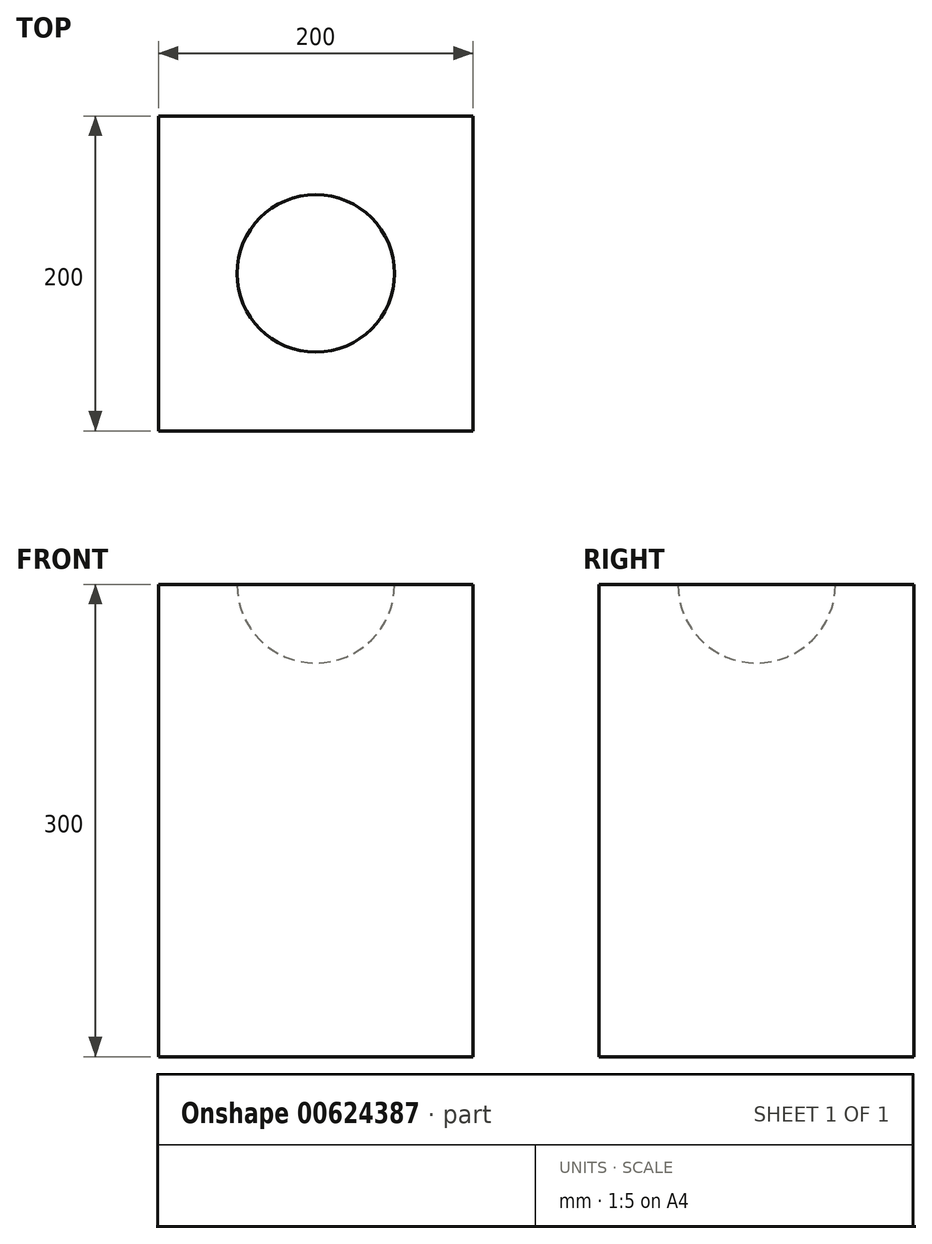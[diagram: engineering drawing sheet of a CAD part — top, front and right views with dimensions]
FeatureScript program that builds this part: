
annotation { "Feature Type Name" : "Feature", "Feature Type Description" : "" }
export const myFeature = defineFeature(function(context is Context, id is Id, definition is map)
    precondition{}
    {
        {
            var Q0;
            Q0=qCreatedBy(makeId("Top.planeOp"),FACE);
            var sketch = newSketch(context, id + "F0", { "sketchPlane" : qUnion([Q0])});
            skLineSegment(sketch, "E0.bottom", {"start": v(100, 100) * mm, "end": v(-100, 100) * mm});
            skLineSegment(sketch, "E0.top", {"start": v(100, -100) * mm, "end": v(-100, -100) * mm});
            skLineSegment(sketch, "E0.left", {"start": v(100, 100) * mm, "end": v(100, -100) * mm});
            skLineSegment(sketch, "E0.right", {"start": v(-100, 100) * mm, "end": v(-100, -100) * mm});
            skPoint(sketch, "E0.middle", {"position": v(0, 0) * mm});
            skSolve(sketch);
        }
        {
            var Q0;
            Q0=makeQuery(id+"F0.imprint","IMPRINT",FACE,{"disambiguationData":[TD([[makeQuery(id+"F0.imprint","IMPRINT",EDGE,{"derivedFrom":sQuery(id+"F0.wireOp",EDGE,"E0.bottom")}),1.0]])]});
            extrude(context, id + "F1", {"entities" : qUnion([Q0]), "depth" : 300 * mm, "offsetDistance" : 25 * mm});
        }
        {
            var Q0;
            Q0=makeQuery(id+"F1.opExtrude","CAP_FACE",FACE,{"disambiguationData":[OSD([sQuery(id+"F0.wireOp",EDGE,"E0.bottom"),sQuery(id+"F0.wireOp",EDGE,"E0.top"),sQuery(id+"F0.wireOp",EDGE,"E0.left"),sQuery(id+"F0.wireOp",EDGE,"E0.right")])],"isStart":false});
            var sketch = newSketch(context, id + "F2", { "sketchPlane" : qUnion([Q0])});
            skArc(sketch, "E1", {"start": v(50, 0) * mm, "mid": v(0, 50) * mm, "end": v(-50, 0) * mm});
            skLineSegment(sketch, "E2", {"start": v(-50, 0) * mm, "end": v(50, 0) * mm});
            skSolve(sketch);
        }
        {
            var Q0;
            Q0=makeQuery(id+"F2.imprint","IMPRINT",FACE,{"disambiguationData":[TD([[makeQuery(id+"F2.imprint","IMPRINT",EDGE,{"derivedFrom":sQuery(id+"F2.wireOp",EDGE,"E1")}),1.0]])]});
            var Q1;
            Q1=sQuery(id+"F2.wireOp",EDGE,"E2");
            revolve(context, id + "F3", {"operationType" : NewBodyOperationType.REMOVE, "entities" : qUnion([Q0]), "axis" : qUnion([Q1]), "revolveType" : RevolveType.FULL, "oppositeDirection" : true});
        }
    });
